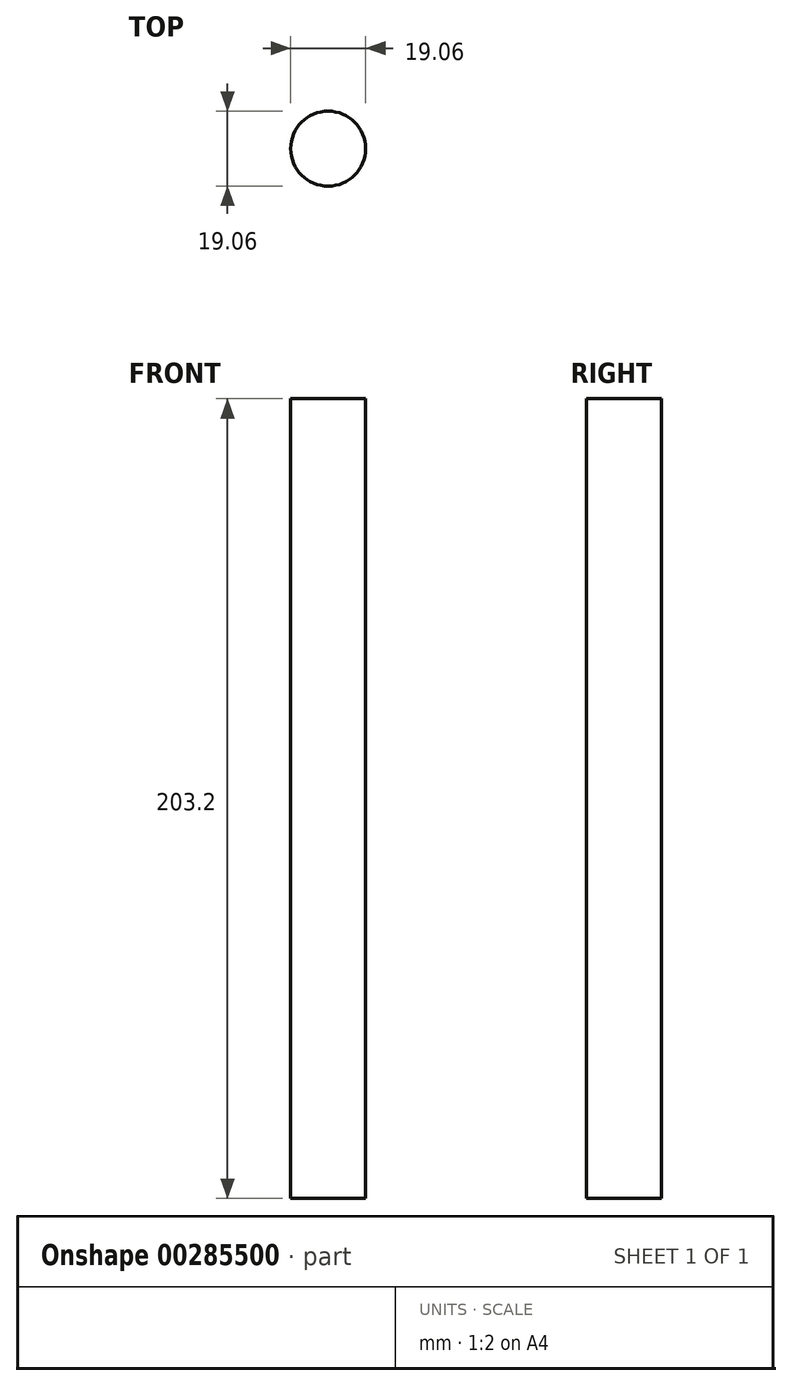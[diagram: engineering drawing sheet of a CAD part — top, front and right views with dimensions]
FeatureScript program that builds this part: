
annotation { "Feature Type Name" : "Feature", "Feature Type Description" : "" }
export const myFeature = defineFeature(function(context is Context, id is Id, definition is map)
    precondition{}
    {
        {
            var Q0;
            Q0=qCreatedBy(makeId("Top.planeOp"),FACE);
            var sketch = newSketch(context, id + "F0", { "sketchPlane" : qUnion([Q0])});
            skCircle(sketch, "E0", {"center": v(0, 0) * mm, "radius": 9.53 * mm});
            skSolve(sketch);
        }
        {
            var Q0;
            Q0=qSketchRegion(id+"F0",true);
            extrude(context, id + "F1", {"entities" : qUnion([Q0]), "depth" : 203.2 * mm});
        }
    });
